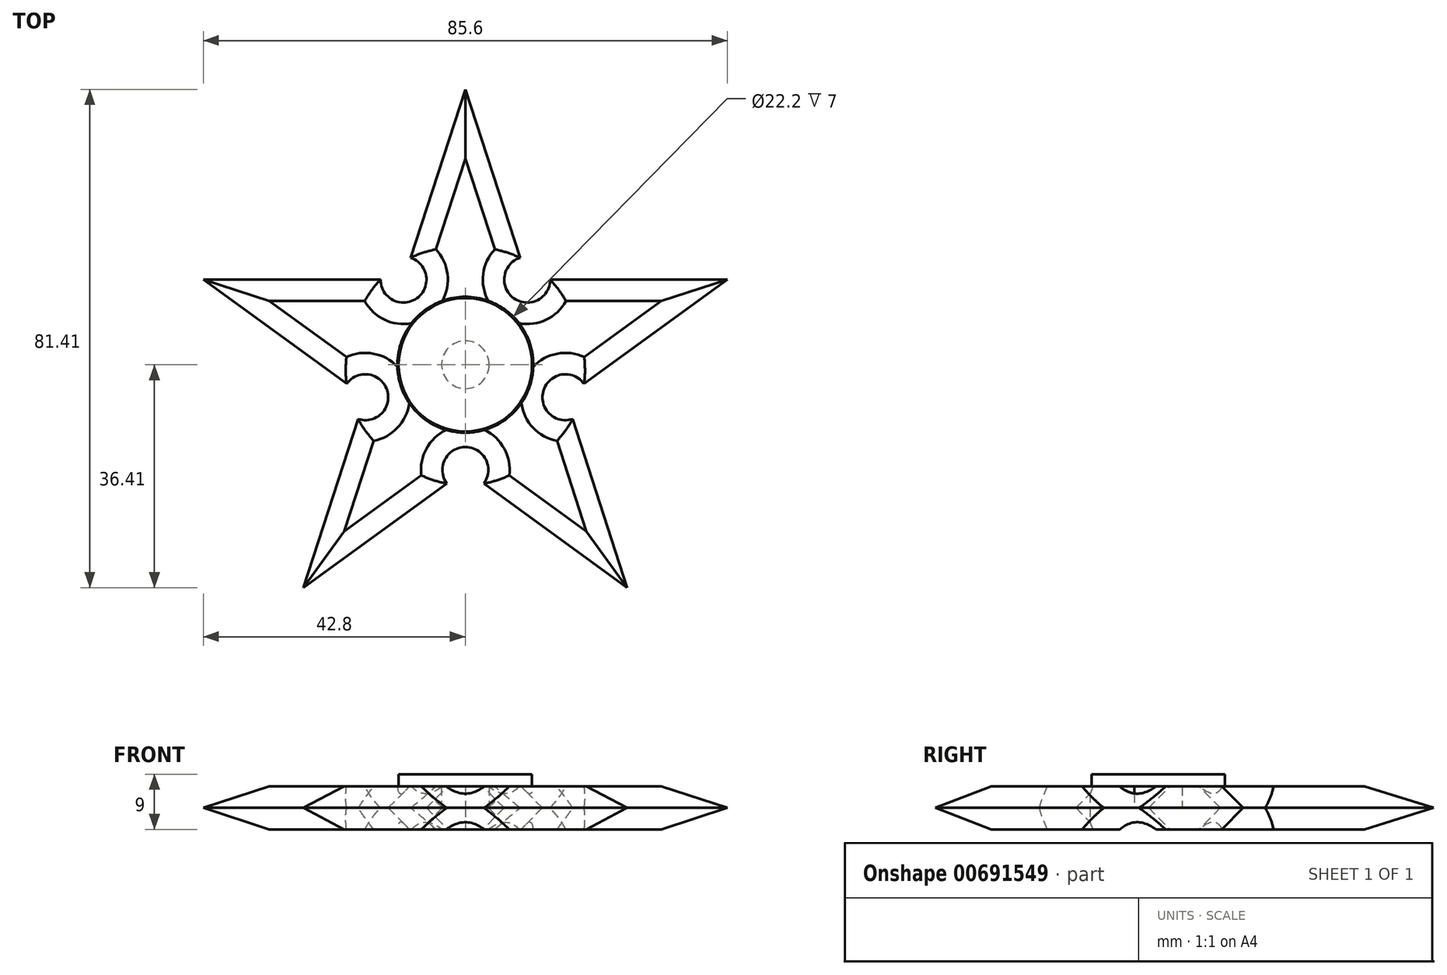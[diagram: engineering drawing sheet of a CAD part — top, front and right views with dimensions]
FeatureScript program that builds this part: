
annotation { "Feature Type Name" : "Feature", "Feature Type Description" : "" }
export const myFeature = defineFeature(function(context is Context, id is Id, definition is map)
    precondition{}
    {
        {
            assignVariable(context, id + "F0", {"name" : "BearingWidth", "anyValue" : 7});
        }
        {
            var Q0;
            Q0=qCreatedBy(makeId("Top.planeOp"),FACE);
            var sketch = newSketch(context, id + "F1", { "sketchPlane" : qUnion([Q0])});
            skCircle(sketch, "E0.cCircle", {"center": v(0, 0) * mm, "radius": 45 * mm, "construction": true});
            skLineSegment(sketch, "E0.0", {"start": v(0, 45) * mm, "end": v(42.8, 13.9) * mm, "construction": true});
            skLineSegment(sketch, "E0.1", {"start": v(42.8, 13.9) * mm, "end": v(26.45, -36.4) * mm, "construction": true});
            skLineSegment(sketch, "E0.2", {"start": v(26.45, -36.4) * mm, "end": v(-26.45, -36.4) * mm, "construction": true});
            skLineSegment(sketch, "E0.3", {"start": v(-26.45, -36.4) * mm, "end": v(-42.8, 13.9) * mm, "construction": true});
            skLineSegment(sketch, "E0.4", {"start": v(-42.8, 13.9) * mm, "end": v(0, 45) * mm, "construction": true});
            skCircle(sketch, "E1.cCircle", {"center": v(0, 0) * mm, "radius": 17.19 * mm, "construction": true});
            skLineSegment(sketch, "E1.0", {"start": v(0, -17.19) * mm, "end": v(-16.35, -5.31) * mm, "construction": true});
            skLineSegment(sketch, "E1.1", {"start": v(-16.35, -5.31) * mm, "end": v(-10.1, 13.9) * mm, "construction": true});
            skLineSegment(sketch, "E1.2", {"start": v(-10.1, 13.9) * mm, "end": v(10.1, 13.9) * mm, "construction": true});
            skLineSegment(sketch, "E1.3", {"start": v(10.1, 13.9) * mm, "end": v(16.35, -5.31) * mm, "construction": true});
            skLineSegment(sketch, "E1.4", {"start": v(16.35, -5.31) * mm, "end": v(0, -17.19) * mm, "construction": true});
            skLineSegment(sketch, "E2", {"start": v(0, 45) * mm, "end": v(-10.1, 13.9) * mm});
            skLineSegment(sketch, "E3", {"start": v(0, 45) * mm, "end": v(10.1, 13.9) * mm});
            skLineSegment(sketch, "E4", {"start": v(10.1, 13.9) * mm, "end": v(42.8, 13.9) * mm});
            skLineSegment(sketch, "E5", {"start": v(42.8, 13.9) * mm, "end": v(16.35, -5.31) * mm});
            skLineSegment(sketch, "E6", {"start": v(16.35, -5.31) * mm, "end": v(26.45, -36.4) * mm});
            skLineSegment(sketch, "E7", {"start": v(0, -17.19) * mm, "end": v(26.45, -36.4) * mm});
            skLineSegment(sketch, "E8", {"start": v(0, -17.19) * mm, "end": v(-26.45, -36.4) * mm});
            skLineSegment(sketch, "E9", {"start": v(-16.35, -5.31) * mm, "end": v(-26.45, -36.4) * mm});
            skLineSegment(sketch, "E10", {"start": v(-10.1, 13.9) * mm, "end": v(-42.8, 13.9) * mm});
            skLineSegment(sketch, "E11", {"start": v(-16.35, -5.31) * mm, "end": v(-42.8, 13.9) * mm});
            skCircle(sketch, "E12", {"center": v(0, 0) * mm, "radius": 11.1 * mm});
            skCircle(sketch, "E13", {"center": v(0, 0) * mm, "radius": 3.9 * mm});
            skCircle(sketch, "E14", {"center": v(-16.35, -5.31) * mm, "radius": 3.75 * mm});
            skCircle(sketch, "E15.1.0", {"center": v(0, -17.19) * mm, "radius": 3.75 * mm});
            skCircle(sketch, "E15.2.0", {"center": v(16.35, -5.31) * mm, "radius": 3.75 * mm});
            skCircle(sketch, "E15.3.0", {"center": v(10.1, 13.9) * mm, "radius": 3.75 * mm});
            skCircle(sketch, "E15.4.0", {"center": v(-10.1, 13.9) * mm, "radius": 3.75 * mm});
            skSolve(sketch);
        }
        {
            var Q0;
            Q0=makeQuery(id+"F1.imprint","IMPRINT",FACE,{"disambiguationData":[TD([[makeQuery(id+"F1.imprint","IMPRINT",EDGE,{"derivedFrom":sQuery(id+"F1.wireOp",EDGE,"E12")}),-1.0]])]});
            extrude(context, id + "F2", {"entities" : qUnion([Q0]), "endBound" : BoundingType.SYMMETRIC, "depth" : (getVariable(context, 'BearingWidth')) * mm, "offsetDistance" : 25 * mm});
        }
        {
            var Q0;
            Q0=makeQuery(id+"F1.imprint","IMPRINT",FACE,{"disambiguationData":[TD([[makeQuery(id+"F1.imprint","IMPRINT",EDGE,{"derivedFrom":sQuery(id+"F1.wireOp",EDGE,"E13")}),1.0]])]});
            extrude(context, id + "F3", {"entities" : qUnion([Q0]), "depth" : (getVariable(context, 'BearingWidth') / 2) * mm, "offsetDistance" : 25 * mm});
        }
        {
            var Q0;
            Q0=makeQuery(id+"F2.opExtrude","CAP_EDGE",EDGE,{"disambiguationData":[OSD([sQuery(id+"F1.wireOp",EDGE,"E8")])],"isStart":false});
            var Q1;
            Q1=makeQuery(id+"F2.opExtrude","CAP_EDGE",EDGE,{"disambiguationData":[OSD([sQuery(id+"F1.wireOp",EDGE,"E8")])],"isStart":true});
            var Q2;
            Q2=makeQuery(id+"F2.opExtrude","CAP_EDGE",EDGE,{"disambiguationData":[OSD([sQuery(id+"F1.wireOp",EDGE,"E9")])],"isStart":false});
            var Q3;
            Q3=makeQuery(id+"F2.opExtrude","CAP_EDGE",EDGE,{"disambiguationData":[OSD([sQuery(id+"F1.wireOp",EDGE,"E9")])],"isStart":true});
            var Q4;
            Q4=makeQuery(id+"F2.opExtrude","CAP_EDGE",EDGE,{"disambiguationData":[OSD([sQuery(id+"F1.wireOp",EDGE,"E11")])],"isStart":false});
            var Q5;
            Q5=makeQuery(id+"F2.opExtrude","CAP_EDGE",EDGE,{"disambiguationData":[OSD([sQuery(id+"F1.wireOp",EDGE,"E11")])],"isStart":true});
            var Q6;
            Q6=makeQuery(id+"F2.opExtrude","CAP_EDGE",EDGE,{"disambiguationData":[OSD([sQuery(id+"F1.wireOp",EDGE,"E10")])],"isStart":false});
            var Q7;
            Q7=makeQuery(id+"F2.opExtrude","CAP_EDGE",EDGE,{"disambiguationData":[OSD([sQuery(id+"F1.wireOp",EDGE,"E10")])],"isStart":true});
            var Q8;
            Q8=makeQuery(id+"F2.opExtrude","CAP_EDGE",EDGE,{"disambiguationData":[OSD([sQuery(id+"F1.wireOp",EDGE,"E2")])],"isStart":false});
            var Q9;
            Q9=makeQuery(id+"F2.opExtrude","CAP_EDGE",EDGE,{"disambiguationData":[OSD([sQuery(id+"F1.wireOp",EDGE,"E2")])],"isStart":true});
            var Q10;
            Q10=makeQuery(id+"F2.opExtrude","CAP_EDGE",EDGE,{"disambiguationData":[OSD([sQuery(id+"F1.wireOp",EDGE,"E3")])],"isStart":true});
            var Q11;
            Q11=makeQuery(id+"F2.opExtrude","CAP_EDGE",EDGE,{"disambiguationData":[OSD([sQuery(id+"F1.wireOp",EDGE,"E3")])],"isStart":false});
            var Q12;
            Q12=makeQuery(id+"F2.opExtrude","CAP_EDGE",EDGE,{"disambiguationData":[OSD([sQuery(id+"F1.wireOp",EDGE,"E4")])],"isStart":false});
            var Q13;
            Q13=makeQuery(id+"F2.opExtrude","CAP_EDGE",EDGE,{"disambiguationData":[OSD([sQuery(id+"F1.wireOp",EDGE,"E4")])],"isStart":true});
            var Q14;
            Q14=makeQuery(id+"F2.opExtrude","CAP_EDGE",EDGE,{"disambiguationData":[OSD([sQuery(id+"F1.wireOp",EDGE,"E5")])],"isStart":false});
            var Q15;
            Q15=makeQuery(id+"F2.opExtrude","CAP_EDGE",EDGE,{"disambiguationData":[OSD([sQuery(id+"F1.wireOp",EDGE,"E5")])],"isStart":true});
            var Q16;
            Q16=makeQuery(id+"F2.opExtrude","CAP_EDGE",EDGE,{"disambiguationData":[OSD([sQuery(id+"F1.wireOp",EDGE,"E6")])],"isStart":false});
            var Q17;
            Q17=makeQuery(id+"F2.opExtrude","CAP_EDGE",EDGE,{"disambiguationData":[OSD([sQuery(id+"F1.wireOp",EDGE,"E6")])],"isStart":true});
            var Q18;
            Q18=makeQuery(id+"F2.opExtrude","CAP_EDGE",EDGE,{"disambiguationData":[OSD([sQuery(id+"F1.wireOp",EDGE,"E7")])],"isStart":false});
            var Q19;
            Q19=makeQuery(id+"F2.opExtrude","CAP_EDGE",EDGE,{"disambiguationData":[OSD([sQuery(id+"F1.wireOp",EDGE,"E7")])],"isStart":true});
            var Q20;
            Q20=makeQuery(id+"F2.opExtrude","CAP_EDGE",EDGE,{"disambiguationData":[OSD([sQuery(id+"F1.wireOp",EDGE,"E15.4.0")])],"isStart":true});
            var Q21;
            Q21=makeQuery(id+"F2.opExtrude","CAP_EDGE",EDGE,{"disambiguationData":[OSD([sQuery(id+"F1.wireOp",EDGE,"E15.4.0")])],"isStart":false});
            var Q22;
            Q22=makeQuery(id+"F2.opExtrude","CAP_EDGE",EDGE,{"disambiguationData":[OSD([sQuery(id+"F1.wireOp",EDGE,"E15.3.0")])],"isStart":true});
            var Q23;
            Q23=makeQuery(id+"F2.opExtrude","CAP_EDGE",EDGE,{"disambiguationData":[OSD([sQuery(id+"F1.wireOp",EDGE,"E15.3.0")])],"isStart":false});
            var Q24;
            Q24=makeQuery(id+"F2.opExtrude","CAP_EDGE",EDGE,{"disambiguationData":[OSD([sQuery(id+"F1.wireOp",EDGE,"E15.2.0")])],"isStart":true});
            var Q25;
            Q25=makeQuery(id+"F2.opExtrude","CAP_EDGE",EDGE,{"disambiguationData":[OSD([sQuery(id+"F1.wireOp",EDGE,"E14")])],"isStart":true});
            var Q26;
            Q26=makeQuery(id+"F2.opExtrude","CAP_EDGE",EDGE,{"disambiguationData":[OSD([sQuery(id+"F1.wireOp",EDGE,"E15.1.0")])],"isStart":true});
            var Q27;
            Q27=makeQuery(id+"F2.opExtrude","CAP_EDGE",EDGE,{"disambiguationData":[OSD([sQuery(id+"F1.wireOp",EDGE,"E14")])],"isStart":false});
            var Q28;
            Q28=makeQuery(id+"F2.opExtrude","CAP_EDGE",EDGE,{"disambiguationData":[OSD([sQuery(id+"F1.wireOp",EDGE,"E15.1.0")])],"isStart":false});
            var Q29;
            Q29=makeQuery(id+"F2.opExtrude","CAP_EDGE",EDGE,{"disambiguationData":[OSD([sQuery(id+"F1.wireOp",EDGE,"E15.2.0")])],"isStart":false});
            chamfer(context, id + "F4", {"entities" : qUnion([Q0, Q1, Q2, Q3, Q4, Q5, Q6, Q7, Q8, Q9, Q10, Q11, Q12, Q13, Q14, Q15, Q16, Q17, Q18, Q19, Q20, Q21, Q22, Q23, Q24, Q25, Q26, Q27, Q28, Q29]), "width" : (getVariable(context, 'BearingWidth') / 2) * mm, "tangentPropagation" : true});
        }
        {
            var Q0;
            Q0=makeQuery(id+"F3.opExtrude","CAP_FACE",FACE,{"disambiguationData":[OSD([sQuery(id+"F1.wireOp",EDGE,"E13")])],"isStart":false});
            var sketch = newSketch(context, id + "F5", { "sketchPlane" : qUnion([Q0])});
            skCircle(sketch, "E16", {"center": v(0, 0) * mm, "radius": 10.9 * mm});
            skSolve(sketch);
        }
        {
            var Q0;
            Q0=makeQuery(id+"F5.imprint","IMPRINT",FACE,{"disambiguationData":[TD([[makeQuery(id+"F5.imprint","IMPRINT",EDGE,{"derivedFrom":sQuery(id+"F5.wireOp",EDGE,"E16")}),1.0]])]});
            var Q1;
            Q1=makeQuery(id+"F5.imprint","IMPRINT",FACE,{"disambiguationData":[TD([[makeQuery(id+"F5.imprint","IMPRINT",EDGE,{"derivedFrom":makeQuery(id+"F3.opExtrude","CAP_EDGE",EDGE,{"disambiguationData":[OSD([sQuery(id+"F1.wireOp",EDGE,"E13")])],"isStart":false})}),1.0]])]});
            extrude(context, id + "F6", {"entities" : qUnion([Q0, Q1]), "operationType" : NewBodyOperationType.ADD, "depth" : 2 * mm, "offsetDistance" : 25 * mm});
        }
    });
